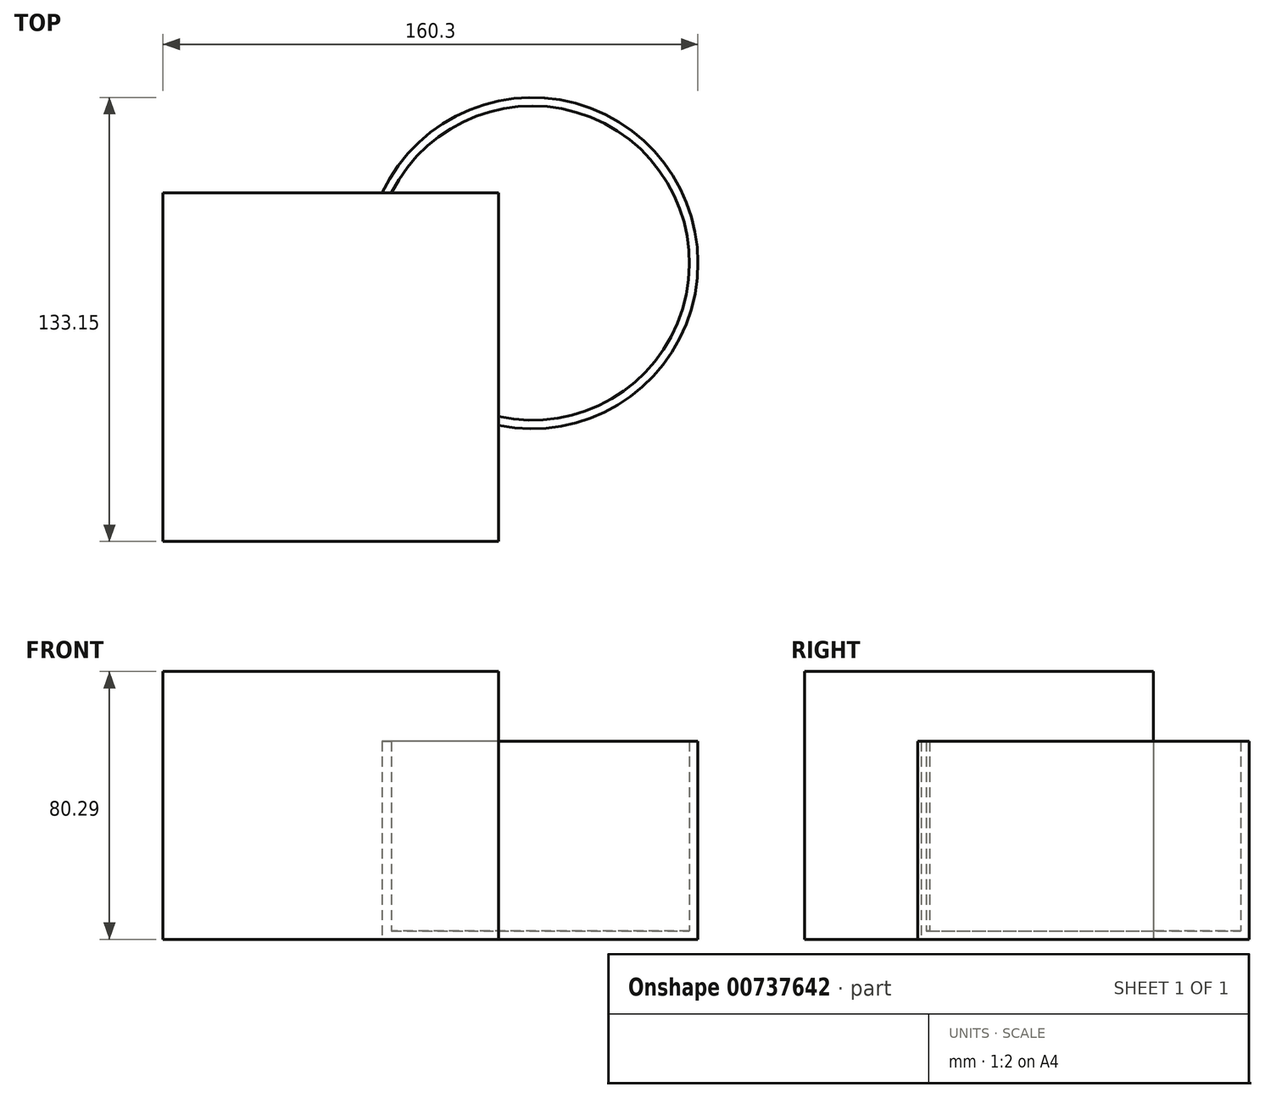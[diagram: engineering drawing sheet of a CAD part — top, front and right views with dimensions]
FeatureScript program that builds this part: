
annotation { "Feature Type Name" : "Feature", "Feature Type Description" : "" }
export const myFeature = defineFeature(function(context is Context, id is Id, definition is map)
    precondition{}
    {
        {
            var Q0;
            Q0=qCreatedBy(makeId("Top.planeOp"),FACE);
            var sketch = newSketch(context, id + "F0", { "sketchPlane" : qUnion([Q0])});
            skCircle(sketch, "E0", {"center": v(0, -10.15) * mm, "radius": 49.65 * mm});
            skSolve(sketch);
        }
        {
            var Q0;
            Q0 = qSketchRegion(id + "F0", true);
            extrude(context, id + "F1", {"entities" : qUnion([Q0]), "depth" : 59.38 * mm, "offsetDistance" : 25.4 * mm});
        }
        {
            var Q0;
            Q0=makeQuery(id+"F1.opExtrude","CAP_FACE",FACE,{"disambiguationData":[OSD([sQuery(id+"F0.wireOp",EDGE,"E0")])],"isStart":false});
            shell(context, id + "F2", {"entities" : qUnion([Q0]), "thickness" : 2.54 * mm});
        }
        {
            var Q0;
            Q0=makeQuery(id+"F1.opExtrude","CAP_FACE",FACE,{"disambiguationData":[OSD([sQuery(id+"F0.wireOp",EDGE,"E0")])],"isStart":true});
            var sketch = newSketch(context, id + "F3", { "sketchPlane" : qUnion([Q0])});
            skLineSegment(sketch, "E1.bottom", {"start": v(-10.05, -10.88) * mm, "end": v(-110.65, -10.88) * mm});
            skLineSegment(sketch, "E1.top", {"start": v(-10.05, 93.65) * mm, "end": v(-110.65, 93.65) * mm});
            skLineSegment(sketch, "E1.left", {"start": v(-10.05, -10.88) * mm, "end": v(-10.05, 93.65) * mm});
            skLineSegment(sketch, "E1.right", {"start": v(-110.65, -10.88) * mm, "end": v(-110.65, 93.65) * mm});
            skSolve(sketch);
        }
        {
            var Q0;
            Q0 = qSketchRegion(id + "F3", true);
            extrude(context, id + "F4", {"entities" : qUnion([Q0]), "operationType" : NewBodyOperationType.ADD, "oppositeDirection" : true, "depth" : 80.3 * mm, "offsetDistance" : 25.4 * mm});
        }
    });
